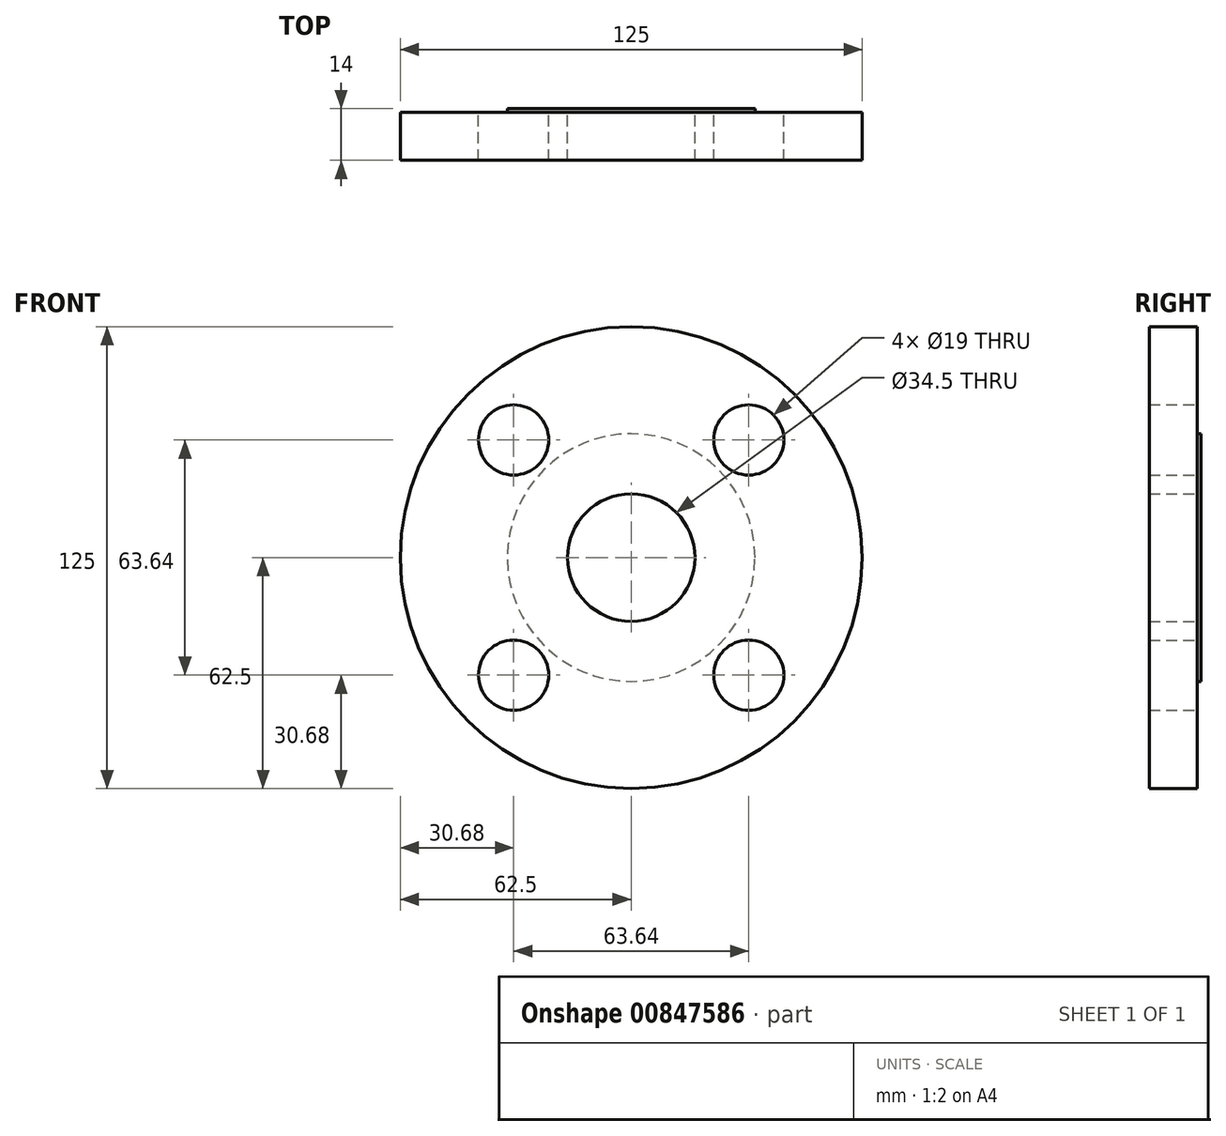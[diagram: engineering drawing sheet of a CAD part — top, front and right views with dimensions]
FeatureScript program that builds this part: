
annotation { "Feature Type Name" : "Feature", "Feature Type Description" : "" }
export const myFeature = defineFeature(function(context is Context, id is Id, definition is map)
    precondition{}
    {
        {
            var Q0;
            Q0=qCreatedBy(makeId("Front.planeOp"),FACE);
            var sketch = newSketch(context, id + "F0", { "sketchPlane" : qUnion([Q0])});
            skLineSegment(sketch, "E0", {"start": v(0, 128.5) * mm, "end": v(0, -143.3) * mm, "construction": true});
            skLineSegment(sketch, "E1", {"start": v(-175.9, 0) * mm, "end": v(185.68, 0) * mm, "construction": true});
            skCircle(sketch, "E2", {"center": v(0, 0) * mm, "radius": 62.5 * mm});
            skCircle(sketch, "E3", {"center": v(0, 0) * mm, "radius": 17.25 * mm});
            skSolve(sketch);
        }
        {
            var Q0;
            Q0 = qSketchRegion(id + "F0", true);
            extrude(context, id + "F1", {"entities" : qUnion([Q0]), "depth" : 14 * mm, "offsetDistance" : 25 * mm});
        }
        {
            var Q0;
            Q0=makeQuery(id+"F1.opExtrude","CAP_FACE",FACE,{"disambiguationData":[OSD([sQuery(id+"F0.wireOp",EDGE,"E2"),sQuery(id+"F0.wireOp",EDGE,"E3")])],"isStart":true});
            var sketch = newSketch(context, id + "F2", { "sketchPlane" : qUnion([Q0])});
            skCircle(sketch, "E4", {"center": v(0, 0) * mm, "radius": 33.5 * mm});
            skCircle(sketch, "E5.0", {"center": v(0, 0) * mm, "radius": 62.5 * mm});
            skSolve(sketch);
        }
        {
            var Q0;
            Q0 = qSketchRegion(id + "F2", true);
            extrude(context, id + "F3", {"entities" : qUnion([Q0]), "operationType" : NewBodyOperationType.REMOVE, "oppositeDirection" : true, "depth" : 1 * mm, "offsetDistance" : 25 * mm});
        }
        {
            var Q0;
            Q0=makeQuery(id+"F1.opExtrude","CAP_FACE",FACE,{"disambiguationData":[OSD([sQuery(id+"F0.wireOp",EDGE,"E2"),sQuery(id+"F0.wireOp",EDGE,"E3")])],"isStart":true});
            var sketch = newSketch(context, id + "F4", { "sketchPlane" : qUnion([Q0])});
            skCircle(sketch, "E6", {"center": v(0, 0) * mm, "radius": 45 * mm, "construction": true});
            skLineSegment(sketch, "E7", {"start": v(87.1, 87.1) * mm, "end": v(-90.37, -90.37) * mm, "construction": true});
            skLineSegment(sketch, "E8.MirrorCS", {"start": v(102.7, 0) * mm, "end": v(-106.73, 0) * mm, "construction": true});
            skLineSegment(sketch, "E9.MirrorCS", {"start": v(0, 103) * mm, "end": v(0, -95.38) * mm, "construction": true});
            skLineSegment(sketch, "E10.MirrorCS", {"start": v(-87.1, 87.1) * mm, "end": v(90.37, -90.37) * mm, "construction": true});
            skCircle(sketch, "E11", {"center": v(-31.82, 31.82) * mm, "radius": 9.5 * mm});
            skCircle(sketch, "E12.1.0", {"center": v(-31.82, -31.82) * mm, "radius": 9.5 * mm});
            skCircle(sketch, "E12.2.0", {"center": v(31.82, -31.82) * mm, "radius": 9.5 * mm});
            skCircle(sketch, "E12.3.0", {"center": v(31.82, 31.82) * mm, "radius": 9.5 * mm});
            skSolve(sketch);
        }
        {
            var Q0;
            Q0 = qSketchRegion(id + "F4", true);
            extrude(context, id + "F5", {"entities" : qUnion([Q0]), "operationType" : NewBodyOperationType.REMOVE, "endBound" : BoundingType.THROUGH_ALL, "oppositeDirection" : true, "depth" : 25 * mm, "offsetDistance" : 25 * mm});
        }
    });
